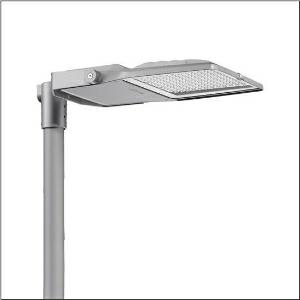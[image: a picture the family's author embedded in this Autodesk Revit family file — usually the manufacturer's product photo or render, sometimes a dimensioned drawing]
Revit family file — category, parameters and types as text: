
# Revit family: floodlight_fl_21_midi___pl43_5xa7782e4a3a_e104
name_source: partatom
category: Lighting Fixtures
units: mm (PartAtom-declared; Revit-internal decimal feet)

## family parameters
Cut with Voids When Loaded = No
Host = Face
Light Source = No
Part Type = Normal
Room Calculation Point = No
Round Connector Dimension = Use Diameter
Shared = No

## types (1)
- --- (1 x LED, 28730 lm, 208.1 W, 4000K)
    Apparent Load = 208 VA
    CIE Flux Codes = 27 78 99 100 100
    Color Rendering = 70
    Color Temperature = 4000K
    Default Elevation = 1800 mm
    Description = Floodlight FL 21 midi, floodlight, primary light control with lens, of PMMA, primary optical cover: protective disc, of toughened safety glass, transparent, light distribution: PL43, light emission: direct distribution, installation type: surface-mounted, LED, High Power LED, rated luminous flux: 28.730lm, luminous efficacy: 138lm/W, light colour: 740, colour temperature: 4000K, control gear: ECG iQ, control: optimised constant luminous flux control (CLO 2.0), Desk-Remote (wireless, voltage-free reading and setting of iQ features in the workshop via application-optimized NFC function/RFID function), Smart-Wire, Night-Set, Temp-Guard, Auto-Match, Street-Remote, with terminal, 6-pole, mains connection: 220..240V, AC, 50/60Hz, start of lifetime: 208W, end of lifetime: 227W, reduction: 90W, luminaire housing, of diecast aluminium, powder-coated, Siteco® metallic grey (DB 702S), corrosivity category C5 according to DIN EN ISO 12944, mast bracket, of steel, galvanised, powder-coated, Siteco® metallic grey (DB 702S), protection rating (complete): IP66, insulation class (complete): insulation class II (safety insulation), certification: CE, protection symbol: D, impact resistance: IK08, permissible operating ambient temperature: -40..+40°C, permissible operating ambient temperature for outdoor applications: -40..+50°C, standard: DIN EN 12944, packaging unit: 1 piece

Light Distribution: PL43
    Height = 76 mm
    Lamp = 1 x LED
    Lamp Light Flux = 28730 lm
    Lamp Power = 208.1 W
    Lamp count = 1
    Length = 657 mm
    Luminous efficacy = 138 lm/W
    Manufacturer = Siteco
    ModVariant = No
    Model = 5XA7782E4A3A
    Number of Poles = 1
    OnlyDefault = Yes
    Power Factor = 1
    Product Name = Floodlight FL 21 midi | PL43
    Product group = floodlight | pylon top
    ProductGroupID = 6101
    Protection Class = Protection class II
    Protection Degree = IP 66
    RLX_Detail_Level = 1
    RlxData = <blob elided: 153269 chars, md5=a70f7ae2>
    Socket = socket
    Standby Power = 0 W
    System Light Flux = 28730 lm
    System Power = 208 W
    Type Comments = factory setting: luminous flux: 100 % | dim-lin: 254 | 710 mA
    Type Image = l_1007123.jpg
    URL = http://relux.com
    VarID = @adj_013677
    Voltage = 0 V
    Weight = 0.00 kg
    Width = 442 mm

## geometry (parser evidence)
native form markers: Blend x4, Sweep x12
no freeform markers — native parametric forms only
